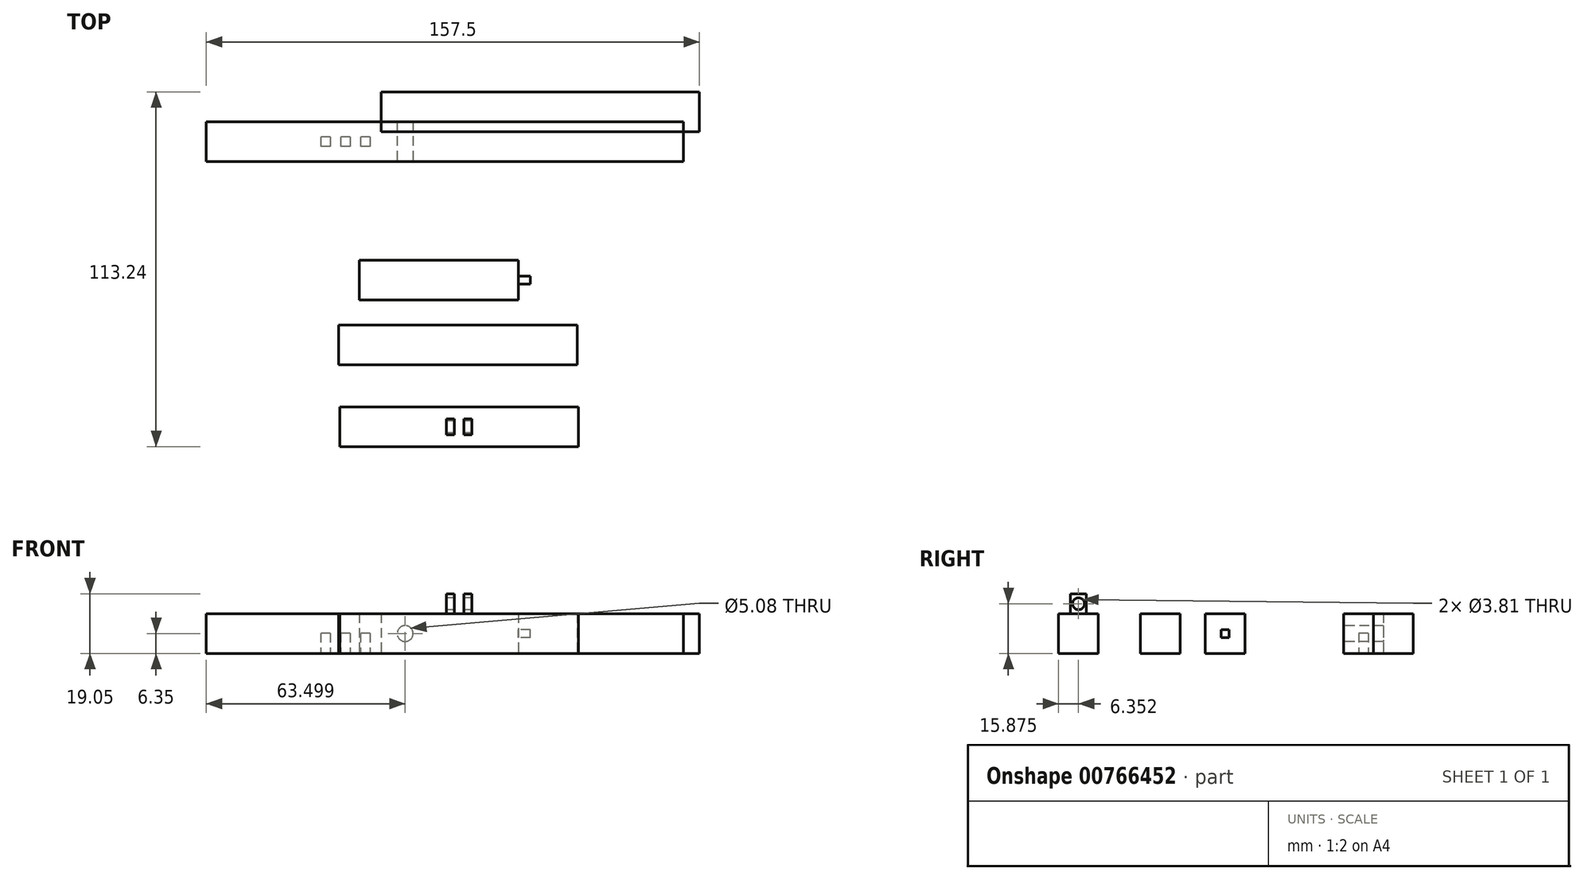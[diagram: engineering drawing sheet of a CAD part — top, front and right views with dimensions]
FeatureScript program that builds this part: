
annotation { "Feature Type Name" : "Feature", "Feature Type Description" : "" }
export const myFeature = defineFeature(function(context is Context, id is Id, definition is map)
    precondition{}
    {
        {
            var Q0;
            Q0=qCreatedBy(makeId("Top.planeOp"),FACE);
            var sketch = newSketch(context, id + "F0", { "sketchPlane" : qUnion([Q0])});
            skLineSegment(sketch, "E0.bottom", {"start": v(-65.93, 47.76) * mm, "end": v(86.47, 47.76) * mm});
            skLineSegment(sketch, "E0.top", {"start": v(-65.93, 35.06) * mm, "end": v(86.47, 35.06) * mm});
            skLineSegment(sketch, "E0.left", {"start": v(-65.93, 47.76) * mm, "end": v(-65.93, 35.06) * mm});
            skLineSegment(sketch, "E0.right", {"start": v(86.47, 47.76) * mm, "end": v(86.47, 35.06) * mm});
            skSolve(sketch);
        }
        {
            var Q0;
            Q0 = qSketchRegion(id + "F0", true);
            extrude(context, id + "F1", {"entities" : qUnion([Q0]), "depth" : 12.7 * mm, "offsetDistance" : 25.4 * mm});
        }
        {
            var Q0;
            Q0=qCreatedBy(makeId("Top.planeOp"),FACE);
            var sketch = newSketch(context, id + "F2", { "sketchPlane" : qUnion([Q0])});
            skLineSegment(sketch, "E1.bottom", {"start": v(-23.73, -17.18) * mm, "end": v(52.47, -17.18) * mm});
            skLineSegment(sketch, "E1.top", {"start": v(-23.73, -29.88) * mm, "end": v(52.47, -29.88) * mm});
            skLineSegment(sketch, "E1.left", {"start": v(-23.73, -17.18) * mm, "end": v(-23.73, -29.88) * mm});
            skLineSegment(sketch, "E1.right", {"start": v(52.47, -17.18) * mm, "end": v(52.47, -29.88) * mm});
            skSolve(sketch);
        }
        {
            var Q0;
            Q0=makeQuery(id+"F2.imprint","IMPRINT",FACE,{"disambiguationData":[TD([[makeQuery(id+"F2.imprint","IMPRINT",EDGE,{"derivedFrom":sQuery(id+"F2.wireOp",EDGE,"E1.bottom")}),-1.0]])]});
            extrude(context, id + "F3", {"entities" : qUnion([Q0]), "depth" : 12.7 * mm, "offsetDistance" : 25.4 * mm});
        }
        {
            var Q0;
            Q0=qCreatedBy(makeId("Top.planeOp"),FACE);
            var sketch = newSketch(context, id + "F4", { "sketchPlane" : qUnion([Q0])});
            skLineSegment(sketch, "E2.bottom", {"start": v(-10.03, 57.29) * mm, "end": v(91.57, 57.29) * mm});
            skLineSegment(sketch, "E2.top", {"start": v(-10.03, 44.59) * mm, "end": v(91.57, 44.59) * mm});
            skLineSegment(sketch, "E2.left", {"start": v(-10.03, 57.29) * mm, "end": v(-10.03, 44.59) * mm});
            skLineSegment(sketch, "E2.right", {"start": v(91.57, 57.29) * mm, "end": v(91.57, 44.59) * mm});
            skSolve(sketch);
        }
        {
            var Q0;
            Q0=qCreatedBy(makeId("Top.planeOp"),FACE);
            var sketch = newSketch(context, id + "F5", { "sketchPlane" : qUnion([Q0])});
            skLineSegment(sketch, "E3.bottom", {"start": v(-17.12, 3.6) * mm, "end": v(33.68, 3.6) * mm});
            skLineSegment(sketch, "E3.top", {"start": v(-17.12, -9.1) * mm, "end": v(33.68, -9.1) * mm});
            skLineSegment(sketch, "E3.left", {"start": v(-17.12, 3.6) * mm, "end": v(-17.12, -9.1) * mm});
            skLineSegment(sketch, "E3.right", {"start": v(33.68, 3.6) * mm, "end": v(33.68, -9.1) * mm});
            skSolve(sketch);
        }
        {
            var Q0;
            Q0=makeQuery(id+"F4.imprint","IMPRINT",FACE,{"disambiguationData":[TD([[makeQuery(id+"F4.imprint","IMPRINT",EDGE,{"derivedFrom":sQuery(id+"F4.wireOp",EDGE,"E2.bottom")}),-1.0]])]});
            var Q1;
            Q1=makeQuery(id+"F5.imprint","IMPRINT",FACE,{"disambiguationData":[TD([[makeQuery(id+"F5.imprint","IMPRINT",EDGE,{"derivedFrom":sQuery(id+"F5.wireOp",EDGE,"E3.bottom")}),-1.0]])]});
            extrude(context, id + "F6", {"entities" : qUnion([Q0, Q1]), "depth" : 12.7 * mm, "offsetDistance" : 25.4 * mm});
        }
        {
            var Q0;
            Q0=makeQuery(id+"F1.opExtrude","SWEPT_FACE",FACE,{"disambiguationData":[OSD([sQuery(id+"F0.wireOp",EDGE,"E0.top")])]});
            var sketch = newSketch(context, id + "F7", { "sketchPlane" : qUnion([Q0])});
            skPoint(sketch, "E4", {"position": v(-2.43, 6.35) * mm});
            skSolve(sketch);
        }
        {
            var Q0;
            Q0=sQuery(id+"F7.wireOp",VERTEX,"E4");
            var Q1;
            Q1=makeQuery(id+"F1.opExtrude","SWEPT_BODY",BODY,{"disambiguationData":[OSD([sQuery(id+"F0.wireOp",EDGE,"E0.bottom"),sQuery(id+"F0.wireOp",EDGE,"E0.top"),sQuery(id+"F0.wireOp",EDGE,"E0.left"),sQuery(id+"F0.wireOp",EDGE,"E0.right")])]});
            hole(context, id + "F8", {"style" : HoleStyle.SIMPLE, "endStyle" : HoleEndStyle.THROUGH, "holeDiameter" : 5.08 * mm, "majorDiameter" : 6.35 * mm, "isTappedThrough" : true, "tappedDepth" : 12.7 * mm, "tapClearance" : 3, "locations" : qUnion([Q0]), "scope" : qUnion([Q1])});
        }
        {
            var Q0;
            Q0=makeQuery(id+"F6.opExtrude","SWEPT_FACE",FACE,{"disambiguationData":[OSD([sQuery(id+"F5.wireOp",EDGE,"E3.right")])]});
            var sketch = newSketch(context, id + "F9", { "sketchPlane" : qUnion([Q0])});
            skLineSegment(sketch, "E5.bottom", {"start": v(-1.48, 5.08) * mm, "end": v(-4.02, 5.08) * mm});
            skLineSegment(sketch, "E5.top", {"start": v(-1.48, 7.62) * mm, "end": v(-4.02, 7.62) * mm});
            skLineSegment(sketch, "E5.left", {"start": v(-1.48, 5.08) * mm, "end": v(-1.48, 7.62) * mm});
            skLineSegment(sketch, "E5.right", {"start": v(-4.02, 5.08) * mm, "end": v(-4.02, 7.62) * mm});
            skPoint(sketch, "E5.middle", {"position": v(-2.75, 6.35) * mm});
            skSolve(sketch);
        }
        {
            var Q0;
            Q0=makeQuery(id+"F9.imprint","IMPRINT",FACE,{"disambiguationData":[TD([[makeQuery(id+"F9.imprint","IMPRINT",EDGE,{"derivedFrom":sQuery(id+"F9.wireOp",EDGE,"E5.bottom")}),-1.0]])]});
            extrude(context, id + "F10", {"entities" : qUnion([Q0]), "operationType" : NewBodyOperationType.ADD, "depth" : 3.8 * mm, "offsetDistance" : 25.4 * mm});
        }
        {
            var Q0;
            Q0=makeQuery(id+"F0.imprint","IMPRINT",FACE,{"disambiguationData":[TD([[makeQuery(id+"F0.imprint","IMPRINT",EDGE,{"derivedFrom":sQuery(id+"F0.wireOp",EDGE,"E0.bottom")}),-1.0]])]});
            var sketch = newSketch(context, id + "F11", { "sketchPlane" : qUnion([Q0])});
            skLineSegment(sketch, "E6.bottom", {"start": v(-19.96, 42.93) * mm, "end": v(-23, 42.93) * mm});
            skLineSegment(sketch, "E6.top", {"start": v(-19.96, 39.89) * mm, "end": v(-23, 39.89) * mm});
            skLineSegment(sketch, "E6.left", {"start": v(-19.96, 42.93) * mm, "end": v(-19.96, 39.89) * mm});
            skLineSegment(sketch, "E6.right", {"start": v(-23, 42.93) * mm, "end": v(-23, 39.89) * mm});
            skPoint(sketch, "E6.middle", {"position": v(-21.48, 41.41) * mm});
            skLineSegment(sketch, "E7.bottom", {"start": v(-13.6, 42.93) * mm, "end": v(-16.65, 42.93) * mm});
            skLineSegment(sketch, "E7.top", {"start": v(-13.6, 39.89) * mm, "end": v(-16.65, 39.89) * mm});
            skLineSegment(sketch, "E7.left", {"start": v(-13.6, 42.93) * mm, "end": v(-13.6, 39.89) * mm});
            skLineSegment(sketch, "E7.right", {"start": v(-16.65, 42.93) * mm, "end": v(-16.65, 39.89) * mm});
            skPoint(sketch, "E7.middle", {"position": v(-15.13, 41.41) * mm});
            skLineSegment(sketch, "E8.bottom", {"start": v(-26.3, 42.93) * mm, "end": v(-29.35, 42.93) * mm});
            skLineSegment(sketch, "E8.top", {"start": v(-26.3, 39.89) * mm, "end": v(-29.35, 39.89) * mm});
            skLineSegment(sketch, "E8.left", {"start": v(-26.3, 42.93) * mm, "end": v(-26.3, 39.89) * mm});
            skLineSegment(sketch, "E8.right", {"start": v(-29.35, 42.93) * mm, "end": v(-29.35, 39.89) * mm});
            skPoint(sketch, "E8.middle", {"position": v(-27.83, 41.41) * mm});
            skSolve(sketch);
        }
        {
            var Q0;
            Q0=makeQuery(id+"F11.imprint","IMPRINT",FACE,{"disambiguationData":[TD([[makeQuery(id+"F11.imprint","IMPRINT",EDGE,{"derivedFrom":sQuery(id+"F11.wireOp",EDGE,"E6.bottom")}),1.0]])]});
            extrude(context, id + "F12", {"entities" : qUnion([Q0]), "operationType" : NewBodyOperationType.REMOVE, "depth" : 6.48 * mm, "offsetDistance" : 25.4 * mm});
        }
        {
            var Q0;
            Q0=makeQuery(id+"F11.imprint","IMPRINT",FACE,{"disambiguationData":[TD([[makeQuery(id+"F11.imprint","IMPRINT",EDGE,{"derivedFrom":sQuery(id+"F11.wireOp",EDGE,"E7.bottom")}),1.0]])]});
            extrude(context, id + "F13", {"entities" : qUnion([Q0]), "operationType" : NewBodyOperationType.REMOVE, "depth" : 6.48 * mm, "offsetDistance" : 25.4 * mm});
        }
        {
            var Q0;
            Q0=makeQuery(id+"F11.imprint","IMPRINT",FACE,{"disambiguationData":[TD([[makeQuery(id+"F11.imprint","IMPRINT",EDGE,{"derivedFrom":sQuery(id+"F11.wireOp",EDGE,"E8.bottom")}),1.0]])]});
            extrude(context, id + "F14", {"entities" : qUnion([Q0]), "operationType" : NewBodyOperationType.REMOVE, "depth" : 6.48 * mm, "offsetDistance" : 25.4 * mm});
        }
        {
            var Q0;
            Q0=qCreatedBy(makeId("Top.planeOp"),FACE);
            var sketch = newSketch(context, id + "F15", { "sketchPlane" : qUnion([Q0])});
            skLineSegment(sketch, "E9.bottom", {"start": v(52.88, -55.95) * mm, "end": v(-23.32, -55.95) * mm});
            skLineSegment(sketch, "E9.top", {"start": v(52.88, -43.25) * mm, "end": v(-23.32, -43.25) * mm});
            skLineSegment(sketch, "E9.left", {"start": v(52.88, -55.95) * mm, "end": v(52.88, -43.25) * mm});
            skLineSegment(sketch, "E9.right", {"start": v(-23.32, -55.95) * mm, "end": v(-23.32, -43.25) * mm});
            skPoint(sketch, "E9.middle", {"position": v(14.78, -49.6) * mm});
            skSolve(sketch);
        }
        {
            var Q0;
            Q0=makeQuery(id+"F15.imprint","IMPRINT",FACE,{"disambiguationData":[TD([[makeQuery(id+"F15.imprint","IMPRINT",EDGE,{"derivedFrom":sQuery(id+"F15.wireOp",EDGE,"E9.bottom")}),-1.0]])]});
            extrude(context, id + "F16", {"entities" : qUnion([Q0]), "depth" : 12.7 * mm, "offsetDistance" : 25.4 * mm});
        }
        {
            var Q0;
            Q0=makeQuery(id+"F16.opExtrude","CAP_FACE",FACE,{"disambiguationData":[OSD([sQuery(id+"F15.wireOp",EDGE,"E9.bottom"),sQuery(id+"F15.wireOp",EDGE,"E9.top"),sQuery(id+"F15.wireOp",EDGE,"E9.left"),sQuery(id+"F15.wireOp",EDGE,"E9.right")])],"isStart":false});
            var sketch = newSketch(context, id + "F17", { "sketchPlane" : qUnion([Q0])});
            skLineSegment(sketch, "E10.bottom", {"start": v(13.26, -52.14) * mm, "end": v(10.72, -52.14) * mm});
            skLineSegment(sketch, "E10.top", {"start": v(13.26, -47.06) * mm, "end": v(10.72, -47.06) * mm});
            skLineSegment(sketch, "E10.left", {"start": v(13.26, -52.14) * mm, "end": v(13.26, -47.06) * mm});
            skLineSegment(sketch, "E10.right", {"start": v(10.72, -52.14) * mm, "end": v(10.72, -47.06) * mm});
            skPoint(sketch, "E10.middle", {"position": v(11.99, -49.6) * mm});
            skLineSegment(sketch, "E11.bottom", {"start": v(18.84, -52.14) * mm, "end": v(16.3, -52.14) * mm});
            skLineSegment(sketch, "E11.top", {"start": v(18.84, -47.06) * mm, "end": v(16.3, -47.06) * mm});
            skLineSegment(sketch, "E11.left", {"start": v(18.84, -52.14) * mm, "end": v(18.84, -47.06) * mm});
            skLineSegment(sketch, "E11.right", {"start": v(16.3, -52.14) * mm, "end": v(16.3, -47.06) * mm});
            skPoint(sketch, "E11.middle", {"position": v(17.57, -49.6) * mm});
            skSolve(sketch);
        }
        {
            var Q0;
            Q0=makeQuery(id+"F17.imprint","IMPRINT",FACE,{"disambiguationData":[TD([[makeQuery(id+"F17.imprint","IMPRINT",EDGE,{"derivedFrom":sQuery(id+"F17.wireOp",EDGE,"E10.bottom")}),-1.0]])]});
            extrude(context, id + "F18", {"entities" : qUnion([Q0]), "operationType" : NewBodyOperationType.ADD, "depth" : 6.35 * mm, "offsetDistance" : 25.4 * mm});
        }
        {
            var Q0;
            Q0=makeQuery(id+"F17.imprint","IMPRINT",FACE,{"disambiguationData":[TD([[makeQuery(id+"F17.imprint","IMPRINT",EDGE,{"derivedFrom":sQuery(id+"F17.wireOp",EDGE,"E11.bottom")}),-1.0]])]});
            extrude(context, id + "F19", {"entities" : qUnion([Q0]), "operationType" : NewBodyOperationType.ADD, "depth" : 6.35 * mm, "offsetDistance" : 25.4 * mm});
        }
        {
            var Q0;
            Q0=makeQuery(id+"F18.opExtrude","SWEPT_FACE",FACE,{"disambiguationData":[OSD([sQuery(id+"F17.wireOp",EDGE,"E10.right")])]});
            var sketch = newSketch(context, id + "F20", { "sketchPlane" : qUnion([Q0])});
            skCircle(sketch, "E12", {"center": v(49.6, 15.88) * mm, "radius": 1.9 * mm});
            skSolve(sketch);
        }
        {
            var Q0;
            Q0=makeQuery(id+"F20.imprint","IMPRINT",FACE,{"disambiguationData":[TD([[makeQuery(id+"F20.imprint","IMPRINT",EDGE,{"derivedFrom":sQuery(id+"F20.wireOp",EDGE,"E12")}),1.0]])]});
            var Q1;
            Q1 = qSketchRegion(id + "F20", true);
            extrude(context, id + "F21", {"entities" : qUnion([Q0, Q1]), "operationType" : NewBodyOperationType.REMOVE, "oppositeDirection" : true, "depth" : 10.67 * mm, "offsetDistance" : 25.4 * mm});
        }
    });
